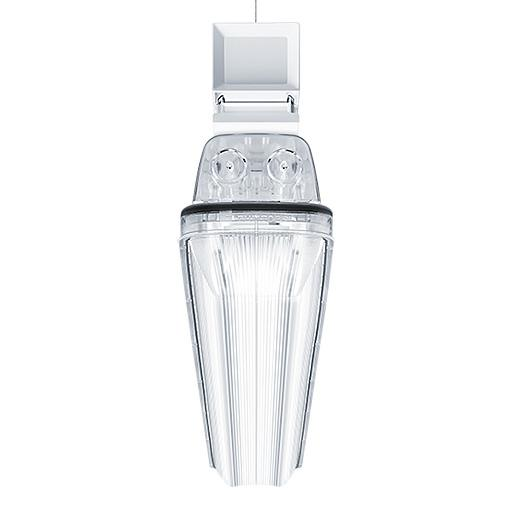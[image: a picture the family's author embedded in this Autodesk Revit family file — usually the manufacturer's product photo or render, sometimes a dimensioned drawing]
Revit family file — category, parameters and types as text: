
# Revit family: Zumtobel TECTON 2 continuous row element AMPHIBIA
name_source: partatom
category: Lighting Fixtures
units: mm (PartAtom-declared; Revit-internal decimal feet)

## family parameters
Cut with Voids When Loaded = No
Host = Face
Light Source = Yes
Maintain Annotation Orientation = No
Part Type = Normal
Room Calculation Point = Yes
Round Connector Dimension = Use Diameter
Shared = No

## types (10) — shared parameters
A = 1500 mm  [stored 4.92126 ft]
Assembly Code = Pr_70_70_48_47
Color Filter = 16777215
Description = Moisture-resistant luminaires
Dimming Lamp Color Temperature Shift = <None>
Emit Shape Visible in Rendering = No
Emit from Rectangle Length = 92 mm  [stored 0.301837 ft]
Emit from Rectangle Width = 1600 mm  [stored 5.24934 ft]
Export Type to IFC As = IfcLightFixtureType
Housing L = Yes
Housing S = No
Lamp = LED
Luminaire Height = 105.81 mm
Luminaire Length = 1600 mm  [stored 5.24934 ft]
Luminaire Width = 92 mm  [stored 0.301837 ft]
Manufacturer = Zumtobel Lighting
Tilt Angle = -90.00°
Type Adapter = Zumtobel-Parts-TECTON 2-Adapter : White
Type Housing = Zumtobel-Parts-AMPHIBIA-Housing : L-1600
Type Housing L = Zumtobel-Parts-AMPHIBIA-Housing : L-1600
Type Housing S = Zumtobel-Parts-AMPHIBIA-Housing : S-1100
Type IFC Predefined Type = DIRECTIONSOURCE
Type Image = ZS_AMP_F_AMPHIBIA_TECTON-II_WH.jpg
URL = https://www.zumtobel.com
zero-valued in all types: Default Elevation

## per-type parameters (varying)
| type | Apparent Load | Model | Photometric Web File | Power Factor |
| AMP L 4600-840 PC WB EVG TEC2 | 30 VA | 42956260 | 42956260_(STD_LEO).IES | 0.93 |
| AMP L 4600-840 PC WB LDO TEC2 | 30 VA | 42956244 | 42956244_(STD_LEO).IES | 0.94 |
| AMP L 6400-840 PC WB EVG TEC2 | 42 VA | 42956251 | 42956251_(STD_LEO).IES | 0.96 |
| AMP L 6400-840 PC WB LDO TEC2 | 42 VA | 42956227 | 42956227_(STD_LEO).IES | 0.96 |
| AMP L 8000-840 PC WB LDO TEC2 | 55 VA | 42956243 | 42956243_(STD_LEO).IES | 0.98 |
| AMP L BAS 4600-840 PC WB EVG TEC2 | 30 VA | 42956249 | 42956249_(STD_LEO).IES | 0.93 |
| AMP L BAS 4600-840 PC WB LDO TEC2 | 30 VA | 42956248 | 42956248_(STD_LEO).IES | 0.94 |
| AMP L BAS 6400-840 PC WB LDO TEC2 | 42 VA | 42956246 | 42956246_(STD_LEO).IES | 0.97 |
| AMP L LT 10000-840 PC WB IVG TEC2 | 70 VA | 42956250 | 42956250_(STD_LEO).IES | 0.97 |
| AMP S 4600-840 PC WB LDO TEC2 | 33 VA | 42956247 | 42956247_(STD_LEO).IES | 0.95 |

note: [stored X ft] marks values corroborated as IEEE doubles in the binary element streams (Revit-internal decimal feet)

## geometry (parser evidence)
native form markers: Sweep x5
no freeform markers — native parametric forms only
